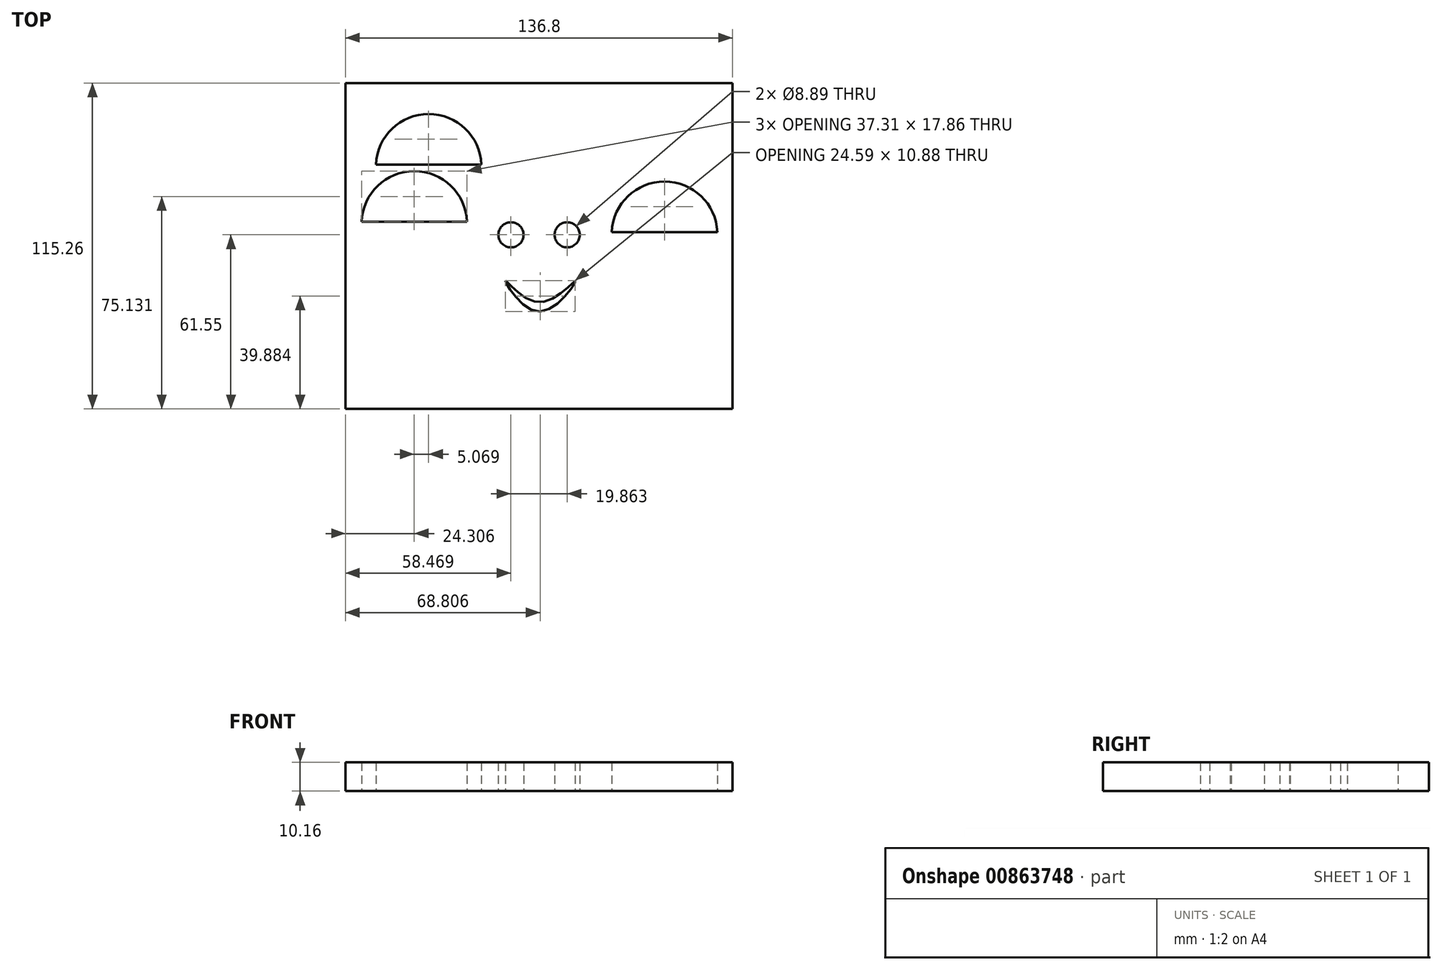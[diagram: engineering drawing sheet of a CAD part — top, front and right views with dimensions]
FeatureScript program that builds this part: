
annotation { "Feature Type Name" : "Feature", "Feature Type Description" : "" }
export const myFeature = defineFeature(function(context is Context, id is Id, definition is map)
    precondition{}
    {
        {
            var Q0;
            Q0=qCreatedBy(makeId("Top.planeOp"),FACE);
            var sketch = newSketch(context, id + "F0", { "sketchPlane" : qUnion([Q0])});
            skLineSegment(sketch, "E0.bottom", {"start": v(-68.4, 64.76) * mm, "end": v(68.4, 64.76) * mm});
            skLineSegment(sketch, "E0.top", {"start": v(-68.4, -50.5) * mm, "end": v(68.4, -50.5) * mm});
            skLineSegment(sketch, "E0.left", {"start": v(-68.4, 64.76) * mm, "end": v(-68.4, -50.5) * mm});
            skLineSegment(sketch, "E0.right", {"start": v(68.4, 64.76) * mm, "end": v(68.4, -50.5) * mm});
            skCircle(sketch, "E1", {"center": v(0, 0) * mm, "radius": 25.41 * mm});
            skArc(sketch, "E2", {"start": v(57.68, 34.27) * mm, "mid": v(39.03, 53.78) * mm, "end": v(20.37, 34.27) * mm});
            skArc(sketch, "E3.MirrorC", {"start": v(-57.68, 35.92) * mm, "mid": v(-39.03, 53.78) * mm, "end": v(-20.37, 35.92) * mm});
            skCircle(sketch, "E4", {"center": v(-9.93, 11.05) * mm, "radius": 4.45 * mm});
            skCircle(sketch, "E5.MirrorC", {"center": v(9.93, 11.05) * mm, "radius": 4.45 * mm});
            skFitSpline(sketch, "E6", {"points": [v(-11.89, -5.18) * mm, v(0, -12.73) * mm, v(12.73, -5.46) * mm, v(0, -16.09) * mm, v(-11.89, -5.18) * mm]});
            skLineSegment(sketch, "E7", {"start": v(-57.68, 35.92) * mm, "end": v(-20.37, 35.92) * mm});
            skLineSegment(sketch, "E8", {"start": v(20.37, 34.27) * mm, "end": v(57.68, 34.27) * mm});
            skArc(sketch, "E9.MirrorC", {"start": v(-62.75, 15.7) * mm, "mid": v(-44.1, 33.56) * mm, "end": v(-25.44, 15.7) * mm});
            skLineSegment(sketch, "E10", {"start": v(-62.75, 15.7) * mm, "end": v(-25.44, 15.7) * mm});
            skArc(sketch, "E11.MirrorC", {"start": v(25.68, 12.06) * mm, "mid": v(44.34, 29.93) * mm, "end": v(63, 12.06) * mm});
            skLineSegment(sketch, "E12", {"start": v(25.68, 12.06) * mm, "end": v(63, 12.06) * mm});
            skSolve(sketch);
        }
        {
            var Q0;
            Q0 = qSketchRegion(id + "F0", true);
            extrude(context, id + "F1", {"entities" : qUnion([Q0]), "depth" : 5.08 * mm, "offsetDistance" : 25.4 * mm});
        }
        {
            var Q0;
            Q0=makeQuery(id+"F0.imprint","IMPRINT",FACE,{"disambiguationData":[TD([[makeQuery(id+"F0.imprint","IMPRINT",EDGE,{"derivedFrom":sQuery(id+"F0.wireOp",EDGE,"E3.MirrorC")}),-1.0]])]});
            var Q1;
            Q1=makeQuery(id+"F0.imprint","IMPRINT",FACE,{"disambiguationData":[TD([[makeQuery(id+"F0.imprint","IMPRINT",EDGE,{"derivedFrom":sQuery(id+"F0.wireOp",EDGE,"E9.MirrorC")}),-1.0]])]});
            var Q2;
            Q2=makeQuery(id+"F0.imprint","IMPRINT",FACE,{"disambiguationData":[TD([[makeQuery(id+"F0.imprint","IMPRINT",EDGE,{"derivedFrom":sQuery(id+"F0.wireOp",EDGE,"E2")}),1.0]])]});
            var Q3;
            Q3=makeQuery(id+"F0.imprint","IMPRINT",FACE,{"disambiguationData":[TD([[makeQuery(id+"F0.imprint","IMPRINT",EDGE,{"derivedFrom":sQuery(id+"F0.wireOp",EDGE,"E11.MirrorC")}),-1.0]])]});
            extrude(context, id + "F2", {"entities" : qUnion([Q0, Q1, Q2, Q3]), "operationType" : NewBodyOperationType.ADD, "depth" : 10.16 * mm, "offsetDistance" : 25.4 * mm});
        }
        {
            var Q0;
            Q0=makeQuery(id+"F0.imprint","IMPRINT",FACE,{"disambiguationData":[TD([[makeQuery(id+"F0.imprint","IMPRINT",EDGE,{"derivedFrom":sQuery(id+"F0.wireOp",EDGE,"E1")}),1.0]])]});
            extrude(context, id + "F3", {"entities" : qUnion([Q0]), "operationType" : NewBodyOperationType.ADD, "depth" : 10.16 * mm, "offsetDistance" : 25.4 * mm});
        }
        {
            var Q0;
            Q0=sQuery(id+"F0.wireOp",EDGE,"E5.MirrorC");
            var Q1;
            Q1=sQuery(id+"F0.wireOp",EDGE,"E4");
            var Q2;
            Q2=sQuery(id+"F0.wireOp",EDGE,"E6");
            extrude(context, id + "F4", {"bodyType" : ToolBodyType.SURFACE, "surfaceEntities" : qUnion([Q0, Q1, Q2]), "depth" : 10.16 * mm, "offsetDistance" : 25.4 * mm});
        }
    });
